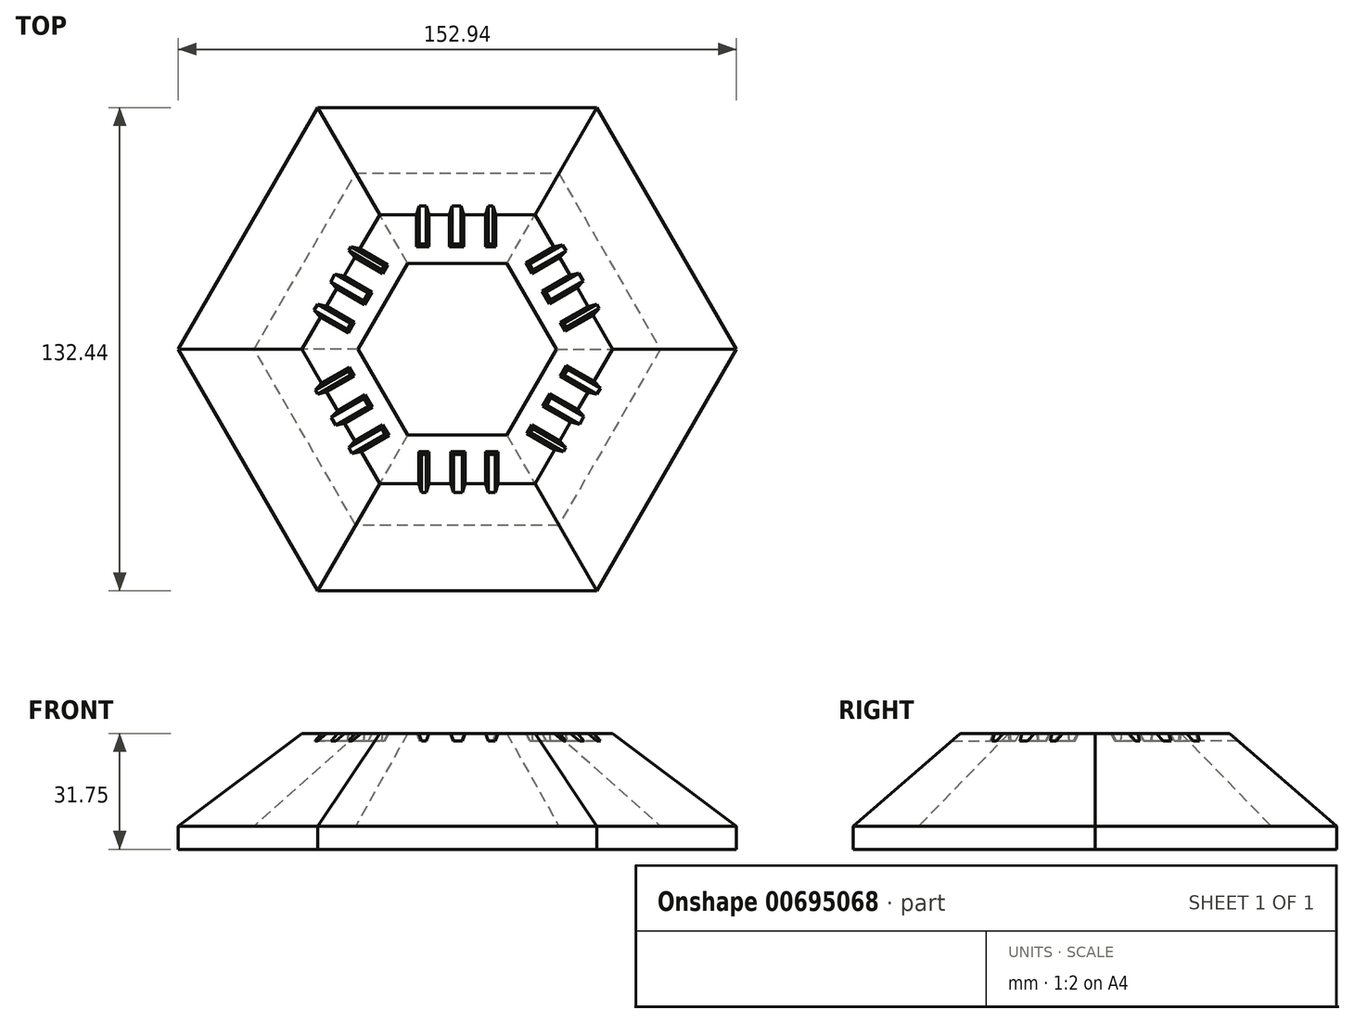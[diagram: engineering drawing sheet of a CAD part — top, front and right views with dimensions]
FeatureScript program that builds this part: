
annotation { "Feature Type Name" : "Feature", "Feature Type Description" : "" }
export const myFeature = defineFeature(function(context is Context, id is Id, definition is map)
    precondition{}
    {
        {
            var Q0;
            Q0=qCreatedBy(makeId("Top.planeOp"),FACE);
            cPlane(context, id + "F0", {"entities" : qUnion([Q0]), "cplaneType" : CPlaneType.OFFSET, "offset" : 25.4 * mm, "width" : 152.4 * mm, "height" : 152.4 * mm});
        }
        {
            var Q0;
            Q0=qCreatedBy(makeId("Top.planeOp"),FACE);
            var sketch = newSketch(context, id + "F1", { "sketchPlane" : qUnion([Q0])});
            skCircle(sketch, "E0.cCircle", {"center": v(0, 0) * mm, "radius": 66.22 * mm, "construction": true});
            skLineSegment(sketch, "E0.0", {"start": v(-38.23, 66.22) * mm, "end": v(38.23, 66.22) * mm});
            skLineSegment(sketch, "E0.1", {"start": v(38.23, 66.22) * mm, "end": v(76.47, 0) * mm});
            skLineSegment(sketch, "E0.2", {"start": v(76.47, 0) * mm, "end": v(38.23, -66.22) * mm});
            skLineSegment(sketch, "E0.3", {"start": v(38.23, -66.22) * mm, "end": v(-38.23, -66.22) * mm});
            skLineSegment(sketch, "E0.4", {"start": v(-38.23, -66.22) * mm, "end": v(-76.47, 0) * mm});
            skLineSegment(sketch, "E0.5", {"start": v(-76.47, 0) * mm, "end": v(-38.23, 66.22) * mm});
            skPoint(sketch, "E0.0.midPoint", {"position": v(0, 66.22) * mm});
            skSolve(sketch);
        }
        {
            var Q0;
            Q0=qCreatedBy(id+"F0.planeOp",FACE);
            var sketch = newSketch(context, id + "F2", { "sketchPlane" : qUnion([Q0])});
            skCircle(sketch, "E1.cCircle", {"center": v(0, 0) * mm, "radius": 36.85 * mm, "construction": true});
            skLineSegment(sketch, "E1.0", {"start": v(-21.28, 36.85) * mm, "end": v(21.28, 36.85) * mm});
            skLineSegment(sketch, "E1.1", {"start": v(21.28, 36.85) * mm, "end": v(42.55, 0) * mm});
            skLineSegment(sketch, "E1.2", {"start": v(42.55, 0) * mm, "end": v(21.28, -36.85) * mm});
            skLineSegment(sketch, "E1.3", {"start": v(21.28, -36.85) * mm, "end": v(-21.28, -36.85) * mm});
            skLineSegment(sketch, "E1.4", {"start": v(-21.28, -36.85) * mm, "end": v(-42.55, 0) * mm});
            skLineSegment(sketch, "E1.5", {"start": v(-42.55, 0) * mm, "end": v(-21.28, 36.85) * mm});
            skPoint(sketch, "E1.0.midPoint", {"position": v(0, 36.85) * mm});
            skSolve(sketch);
        }
        {
            var Q0;
            Q0=makeQuery(id+"F1.imprint","IMPRINT",FACE,{"disambiguationData":[TD([[makeQuery(id+"F1.imprint","IMPRINT",EDGE,{"derivedFrom":sQuery(id+"F1.wireOp",EDGE,"E0.0")}),-1.0]])]});
            var Q1;
            Q1=makeQuery(id+"F2.imprint","IMPRINT",FACE,{"disambiguationData":[TD([[makeQuery(id+"F2.imprint","IMPRINT",EDGE,{"derivedFrom":sQuery(id+"F2.wireOp",EDGE,"E1.0")}),-1.0]])]});
            loft(context, id + "F3", {"sheetProfilesArray" : [{ "sheetProfileEntities" : qUnion([Q0]) }, { "sheetProfileEntities" : qUnion([Q1]) }]});
        }
        {
            var Q0;
            Q0=makeQuery(id+"F3.opLoft","CAP_FACE",FACE,{"disambiguationData":[OSD([makeQuery(id+"F1.imprint","IMPRINT",FACE,{"disambiguationData":[TD([[makeQuery(id+"F1.imprint","IMPRINT",EDGE,{"derivedFrom":sQuery(id+"F1.wireOp",EDGE,"E0.0")}),-1.0]])]})])],"isStart":true});
            extrude(context, id + "F4", {"entities" : qUnion([Q0]), "operationType" : NewBodyOperationType.ADD, "depth" : 6.35 * mm, "offsetDistance" : 25.4 * mm});
        }
        {
            var Q0;
            Q0=qCreatedBy(id+"F0.planeOp",FACE);
            var sketch = newSketch(context, id + "F5", { "sketchPlane" : qUnion([Q0])});
            skCircle(sketch, "E2.cCircle", {"center": v(0, 0) * mm, "radius": 23.52 * mm, "construction": true});
            skLineSegment(sketch, "E2.0", {"start": v(-13.58, 23.52) * mm, "end": v(13.58, 23.52) * mm});
            skLineSegment(sketch, "E2.1", {"start": v(13.58, 23.52) * mm, "end": v(27.15, 0) * mm});
            skLineSegment(sketch, "E2.2", {"start": v(27.15, 0) * mm, "end": v(13.58, -23.52) * mm});
            skLineSegment(sketch, "E2.3", {"start": v(13.58, -23.52) * mm, "end": v(-13.58, -23.52) * mm});
            skLineSegment(sketch, "E2.4", {"start": v(-13.58, -23.52) * mm, "end": v(-27.15, 0) * mm});
            skLineSegment(sketch, "E2.5", {"start": v(-27.15, 0) * mm, "end": v(-13.58, 23.52) * mm});
            skPoint(sketch, "E2.0.midPoint", {"position": v(0, 23.52) * mm});
            skSolve(sketch);
        }
        {
            var Q0;
            Q0=qCreatedBy(makeId("Top.planeOp"),FACE);
            var sketch = newSketch(context, id + "F6", { "sketchPlane" : qUnion([Q0])});
            skCircle(sketch, "E3.cCircle", {"center": v(0, 0) * mm, "radius": 48.2 * mm, "construction": true});
            skLineSegment(sketch, "E3.0", {"start": v(-27.83, 48.2) * mm, "end": v(27.83, 48.2) * mm});
            skLineSegment(sketch, "E3.1", {"start": v(27.83, 48.2) * mm, "end": v(55.66, 0) * mm});
            skLineSegment(sketch, "E3.2", {"start": v(55.66, 0) * mm, "end": v(27.83, -48.2) * mm});
            skLineSegment(sketch, "E3.3", {"start": v(27.83, -48.2) * mm, "end": v(-27.83, -48.2) * mm});
            skLineSegment(sketch, "E3.4", {"start": v(-27.83, -48.2) * mm, "end": v(-55.66, 0) * mm});
            skLineSegment(sketch, "E3.5", {"start": v(-55.66, 0) * mm, "end": v(-27.83, 48.2) * mm});
            skPoint(sketch, "E3.0.midPoint", {"position": v(0, 48.2) * mm});
            skSolve(sketch);
        }
        {
            var Q1;
            Q1=makeQuery(id+"F5.imprint","IMPRINT",FACE,{"disambiguationData":[TD([[makeQuery(id+"F5.imprint","IMPRINT",EDGE,{"derivedFrom":sQuery(id+"F5.wireOp",EDGE,"E2.0")}),-1.0]])]});
            var Q2;
            Q2 = qSketchRegion(id + "F6", true);
            loft(context, id + "F7", {"operationType" : NewBodyOperationType.REMOVE, "sheetProfilesArray" : [{ "sheetProfileEntities" : qUnion([Q1]) }, { "sheetProfileEntities" : qUnion([Q2]) }]});
        }
        {
            var Q0;
            Q0=qCreatedBy(id+"F0.planeOp",FACE);
            var sketch = newSketch(context, id + "F8", { "sketchPlane" : qUnion([Q0])});
            skLineSegment(sketch, "E4", {"start": v(-7.72, -28.07) * mm, "end": v(-7.72, -40.59) * mm});
            skLineSegment(sketch, "E5", {"start": v(7.7, -28.07) * mm, "end": v(7.7, -40.59) * mm});
            skLineSegment(sketch, "E6", {"start": v(-7.72, -28.07) * mm, "end": v(-10.55, -28.07) * mm});
            skLineSegment(sketch, "E7", {"start": v(-10.55, -28.07) * mm, "end": v(-10.55, -40.59) * mm});
            skLineSegment(sketch, "E8", {"start": v(-10.55, -40.59) * mm, "end": v(-7.72, -40.59) * mm});
            skLineSegment(sketch, "E9", {"start": v(7.7, -40.59) * mm, "end": v(11.14, -40.59) * mm});
            skLineSegment(sketch, "E10", {"start": v(11.14, -40.59) * mm, "end": v(11.14, -28.07) * mm});
            skLineSegment(sketch, "E11", {"start": v(11.14, -28.07) * mm, "end": v(7.7, -28.07) * mm});
            skLineSegment(sketch, "E12", {"start": v(-1.82, -28.07) * mm, "end": v(2.14, -28.07) * mm});
            skLineSegment(sketch, "E13", {"start": v(2.14, -28.07) * mm, "end": v(2.14, -40.59) * mm});
            skLineSegment(sketch, "E14", {"start": v(2.14, -40.59) * mm, "end": v(-1.82, -40.59) * mm});
            skLineSegment(sketch, "E15", {"start": v(-1.82, -40.59) * mm, "end": v(-1.82, -28.07) * mm});
            skLineSegment(sketch, "E16.1.0", {"start": v(20.45, -20.72) * mm, "end": v(31.29, -26.98) * mm});
            skLineSegment(sketch, "E16.1.1", {"start": v(28.16, -7.37) * mm, "end": v(39, -13.63) * mm});
            skLineSegment(sketch, "E16.1.2", {"start": v(19.03, -23.17) * mm, "end": v(29.87, -29.43) * mm});
            skLineSegment(sketch, "E16.1.3", {"start": v(40.72, -10.65) * mm, "end": v(29.88, -4.39) * mm});
            skLineSegment(sketch, "E16.1.4", {"start": v(25.38, -12.18) * mm, "end": v(36.22, -18.44) * mm});
            skLineSegment(sketch, "E16.1.5", {"start": v(34.24, -21.87) * mm, "end": v(23.4, -15.61) * mm});
            skLineSegment(sketch, "E16.1.6", {"start": v(20.45, -20.72) * mm, "end": v(19.03, -23.17) * mm});
            skLineSegment(sketch, "E16.1.7", {"start": v(29.88, -4.39) * mm, "end": v(28.16, -7.37) * mm});
            skLineSegment(sketch, "E16.1.8", {"start": v(36.22, -18.44) * mm, "end": v(34.24, -21.87) * mm});
            skLineSegment(sketch, "E16.1.9", {"start": v(29.87, -29.43) * mm, "end": v(31.29, -26.98) * mm});
            skLineSegment(sketch, "E16.1.10", {"start": v(39, -13.63) * mm, "end": v(40.72, -10.65) * mm});
            skLineSegment(sketch, "E16.1.11", {"start": v(23.4, -15.61) * mm, "end": v(25.38, -12.18) * mm});
            skLineSegment(sketch, "E16.2.0", {"start": v(28.17, 7.35) * mm, "end": v(39, 13.6) * mm});
            skLineSegment(sketch, "E16.2.1", {"start": v(20.46, 20.7) * mm, "end": v(31.3, 26.96) * mm});
            skLineSegment(sketch, "E16.2.2", {"start": v(29.59, 4.9) * mm, "end": v(40.42, 11.15) * mm});
            skLineSegment(sketch, "E16.2.3", {"start": v(29.58, 29.94) * mm, "end": v(18.74, 23.68) * mm});
            skLineSegment(sketch, "E16.2.4", {"start": v(23.24, 15.89) * mm, "end": v(34.08, 22.14) * mm});
            skLineSegment(sketch, "E16.2.5", {"start": v(36.06, 18.72) * mm, "end": v(25.22, 12.46) * mm});
            skLineSegment(sketch, "E16.2.6", {"start": v(28.17, 7.35) * mm, "end": v(29.59, 4.9) * mm});
            skLineSegment(sketch, "E16.2.7", {"start": v(18.74, 23.68) * mm, "end": v(20.46, 20.7) * mm});
            skLineSegment(sketch, "E16.2.8", {"start": v(34.08, 22.14) * mm, "end": v(36.06, 18.72) * mm});
            skLineSegment(sketch, "E16.2.9", {"start": v(40.42, 11.15) * mm, "end": v(39, 13.6) * mm});
            skLineSegment(sketch, "E16.2.10", {"start": v(31.3, 26.96) * mm, "end": v(29.58, 29.94) * mm});
            skLineSegment(sketch, "E16.2.11", {"start": v(25.22, 12.46) * mm, "end": v(23.24, 15.89) * mm});
            skLineSegment(sketch, "E16.3.0", {"start": v(7.72, 28.07) * mm, "end": v(7.72, 40.59) * mm});
            skLineSegment(sketch, "E16.3.1", {"start": v(-7.7, 28.07) * mm, "end": v(-7.7, 40.59) * mm});
            skLineSegment(sketch, "E16.3.2", {"start": v(10.55, 28.07) * mm, "end": v(10.55, 40.59) * mm});
            skLineSegment(sketch, "E16.3.3", {"start": v(-11.14, 40.59) * mm, "end": v(-11.14, 28.07) * mm});
            skLineSegment(sketch, "E16.3.4", {"start": v(-2.14, 28.07) * mm, "end": v(-2.14, 40.59) * mm});
            skLineSegment(sketch, "E16.3.5", {"start": v(1.82, 40.59) * mm, "end": v(1.82, 28.07) * mm});
            skLineSegment(sketch, "E16.3.6", {"start": v(7.72, 28.07) * mm, "end": v(10.55, 28.07) * mm});
            skLineSegment(sketch, "E16.3.7", {"start": v(-11.14, 28.07) * mm, "end": v(-7.7, 28.07) * mm});
            skLineSegment(sketch, "E16.3.8", {"start": v(-2.14, 40.59) * mm, "end": v(1.82, 40.59) * mm});
            skLineSegment(sketch, "E16.3.9", {"start": v(10.55, 40.59) * mm, "end": v(7.72, 40.59) * mm});
            skLineSegment(sketch, "E16.3.10", {"start": v(-7.7, 40.59) * mm, "end": v(-11.14, 40.59) * mm});
            skLineSegment(sketch, "E16.3.11", {"start": v(1.82, 28.07) * mm, "end": v(-2.14, 28.07) * mm});
            skLineSegment(sketch, "E16.4.0", {"start": v(-20.45, 20.72) * mm, "end": v(-31.29, 26.98) * mm});
            skLineSegment(sketch, "E16.4.1", {"start": v(-28.16, 7.37) * mm, "end": v(-39, 13.63) * mm});
            skLineSegment(sketch, "E16.4.2", {"start": v(-19.03, 23.17) * mm, "end": v(-29.87, 29.43) * mm});
            skLineSegment(sketch, "E16.4.3", {"start": v(-40.72, 10.65) * mm, "end": v(-29.88, 4.39) * mm});
            skLineSegment(sketch, "E16.4.4", {"start": v(-25.38, 12.18) * mm, "end": v(-36.22, 18.44) * mm});
            skLineSegment(sketch, "E16.4.5", {"start": v(-34.24, 21.87) * mm, "end": v(-23.4, 15.61) * mm});
            skLineSegment(sketch, "E16.4.6", {"start": v(-20.45, 20.72) * mm, "end": v(-19.03, 23.17) * mm});
            skLineSegment(sketch, "E16.4.7", {"start": v(-29.88, 4.39) * mm, "end": v(-28.16, 7.37) * mm});
            skLineSegment(sketch, "E16.4.8", {"start": v(-36.22, 18.44) * mm, "end": v(-34.24, 21.87) * mm});
            skLineSegment(sketch, "E16.4.9", {"start": v(-29.87, 29.43) * mm, "end": v(-31.29, 26.98) * mm});
            skLineSegment(sketch, "E16.4.10", {"start": v(-39, 13.63) * mm, "end": v(-40.72, 10.65) * mm});
            skLineSegment(sketch, "E16.4.11", {"start": v(-23.4, 15.61) * mm, "end": v(-25.38, 12.18) * mm});
            skLineSegment(sketch, "E16.5.0", {"start": v(-28.17, -7.35) * mm, "end": v(-39, -13.6) * mm});
            skLineSegment(sketch, "E16.5.1", {"start": v(-20.46, -20.7) * mm, "end": v(-31.3, -26.96) * mm});
            skLineSegment(sketch, "E16.5.2", {"start": v(-29.59, -4.9) * mm, "end": v(-40.42, -11.15) * mm});
            skLineSegment(sketch, "E16.5.3", {"start": v(-29.58, -29.94) * mm, "end": v(-18.74, -23.68) * mm});
            skLineSegment(sketch, "E16.5.4", {"start": v(-23.24, -15.89) * mm, "end": v(-34.08, -22.14) * mm});
            skLineSegment(sketch, "E16.5.5", {"start": v(-36.06, -18.72) * mm, "end": v(-25.22, -12.46) * mm});
            skLineSegment(sketch, "E16.5.6", {"start": v(-28.17, -7.35) * mm, "end": v(-29.59, -4.9) * mm});
            skLineSegment(sketch, "E16.5.7", {"start": v(-18.74, -23.68) * mm, "end": v(-20.46, -20.7) * mm});
            skLineSegment(sketch, "E16.5.8", {"start": v(-34.08, -22.14) * mm, "end": v(-36.06, -18.72) * mm});
            skLineSegment(sketch, "E16.5.9", {"start": v(-40.42, -11.15) * mm, "end": v(-39, -13.6) * mm});
            skLineSegment(sketch, "E16.5.10", {"start": v(-31.3, -26.96) * mm, "end": v(-29.58, -29.94) * mm});
            skLineSegment(sketch, "E16.5.11", {"start": v(-25.22, -12.46) * mm, "end": v(-23.24, -15.89) * mm});
            skPoint(sketch, "E16.center", {"position": v(0, 0) * mm});
            skSolve(sketch);
        }
        {
            var Q0;
            Q0=makeQuery(id+"F8.imprint","IMPRINT",FACE,{"disambiguationData":[TD([[makeQuery(id+"F8.imprint","IMPRINT",EDGE,{"derivedFrom":sQuery(id+"F8.wireOp",EDGE,"E4")}),-1.0]])]});
            var Q1;
            Q1=makeQuery(id+"F8.imprint","IMPRINT",FACE,{"disambiguationData":[TD([[makeQuery(id+"F8.imprint","IMPRINT",EDGE,{"derivedFrom":sQuery(id+"F8.wireOp",EDGE,"E12")}),-1.0]])]});
            var Q2;
            Q2=makeQuery(id+"F8.imprint","IMPRINT",FACE,{"disambiguationData":[TD([[makeQuery(id+"F8.imprint","IMPRINT",EDGE,{"derivedFrom":sQuery(id+"F8.wireOp",EDGE,"E5")}),1.0]])]});
            var Q3;
            Q3=makeQuery(id+"F8.imprint","IMPRINT",FACE,{"disambiguationData":[TD([[makeQuery(id+"F8.imprint","IMPRINT",EDGE,{"derivedFrom":sQuery(id+"F8.wireOp",EDGE,"E16.5.1")}),1.0]])]});
            var Q4;
            Q4=makeQuery(id+"F8.imprint","IMPRINT",FACE,{"disambiguationData":[TD([[makeQuery(id+"F8.imprint","IMPRINT",EDGE,{"derivedFrom":sQuery(id+"F8.wireOp",EDGE,"E16.5.4")}),-1.0]])]});
            var Q5;
            Q5=makeQuery(id+"F8.imprint","IMPRINT",FACE,{"disambiguationData":[TD([[makeQuery(id+"F8.imprint","IMPRINT",EDGE,{"derivedFrom":sQuery(id+"F8.wireOp",EDGE,"E16.5.0")}),-1.0]])]});
            var Q6;
            Q6=makeQuery(id+"F8.imprint","IMPRINT",FACE,{"disambiguationData":[TD([[makeQuery(id+"F8.imprint","IMPRINT",EDGE,{"derivedFrom":sQuery(id+"F8.wireOp",EDGE,"E16.4.1")}),1.0]])]});
            var Q7;
            Q7=makeQuery(id+"F8.imprint","IMPRINT",FACE,{"disambiguationData":[TD([[makeQuery(id+"F8.imprint","IMPRINT",EDGE,{"derivedFrom":sQuery(id+"F8.wireOp",EDGE,"E16.4.4")}),-1.0]])]});
            var Q8;
            Q8=makeQuery(id+"F8.imprint","IMPRINT",FACE,{"disambiguationData":[TD([[makeQuery(id+"F8.imprint","IMPRINT",EDGE,{"derivedFrom":sQuery(id+"F8.wireOp",EDGE,"E16.4.0")}),-1.0]])]});
            var Q9;
            Q9=makeQuery(id+"F8.imprint","IMPRINT",FACE,{"disambiguationData":[TD([[makeQuery(id+"F8.imprint","IMPRINT",EDGE,{"derivedFrom":sQuery(id+"F8.wireOp",EDGE,"E16.3.1")}),1.0]])]});
            var Q10;
            Q10=makeQuery(id+"F8.imprint","IMPRINT",FACE,{"disambiguationData":[TD([[makeQuery(id+"F8.imprint","IMPRINT",EDGE,{"derivedFrom":sQuery(id+"F8.wireOp",EDGE,"E16.3.4")}),-1.0]])]});
            var Q11;
            Q11=makeQuery(id+"F8.imprint","IMPRINT",FACE,{"disambiguationData":[TD([[makeQuery(id+"F8.imprint","IMPRINT",EDGE,{"derivedFrom":sQuery(id+"F8.wireOp",EDGE,"E16.3.0")}),-1.0]])]});
            var Q12;
            Q12=makeQuery(id+"F8.imprint","IMPRINT",FACE,{"disambiguationData":[TD([[makeQuery(id+"F8.imprint","IMPRINT",EDGE,{"derivedFrom":sQuery(id+"F8.wireOp",EDGE,"E16.2.1")}),1.0]])]});
            var Q13;
            Q13=makeQuery(id+"F8.imprint","IMPRINT",FACE,{"disambiguationData":[TD([[makeQuery(id+"F8.imprint","IMPRINT",EDGE,{"derivedFrom":sQuery(id+"F8.wireOp",EDGE,"E16.2.4")}),-1.0]])]});
            var Q14;
            Q14=makeQuery(id+"F8.imprint","IMPRINT",FACE,{"disambiguationData":[TD([[makeQuery(id+"F8.imprint","IMPRINT",EDGE,{"derivedFrom":sQuery(id+"F8.wireOp",EDGE,"E16.2.0")}),-1.0]])]});
            var Q15;
            Q15=makeQuery(id+"F8.imprint","IMPRINT",FACE,{"disambiguationData":[TD([[makeQuery(id+"F8.imprint","IMPRINT",EDGE,{"derivedFrom":sQuery(id+"F8.wireOp",EDGE,"E16.1.1")}),1.0]])]});
            var Q16;
            Q16=makeQuery(id+"F8.imprint","IMPRINT",FACE,{"disambiguationData":[TD([[makeQuery(id+"F8.imprint","IMPRINT",EDGE,{"derivedFrom":sQuery(id+"F8.wireOp",EDGE,"E16.1.4")}),-1.0]])]});
            var Q17;
            Q17=makeQuery(id+"F8.imprint","IMPRINT",FACE,{"disambiguationData":[TD([[makeQuery(id+"F8.imprint","IMPRINT",EDGE,{"derivedFrom":sQuery(id+"F8.wireOp",EDGE,"E16.1.0")}),-1.0]])]});
            extrude(context, id + "F9", {"entities" : qUnion([Q0, Q1, Q2, Q3, Q4, Q5, Q6, Q7, Q8, Q9, Q10, Q11, Q12, Q13, Q14, Q15, Q16, Q17]), "operationType" : NewBodyOperationType.REMOVE, "oppositeDirection" : true, "depth" : 2.1 * mm, "offsetDistance" : 25.4 * mm, "hasDraft" : true, "draftAngle" : 20 * degree, "draftPullDirection" : true});
        }
    });
